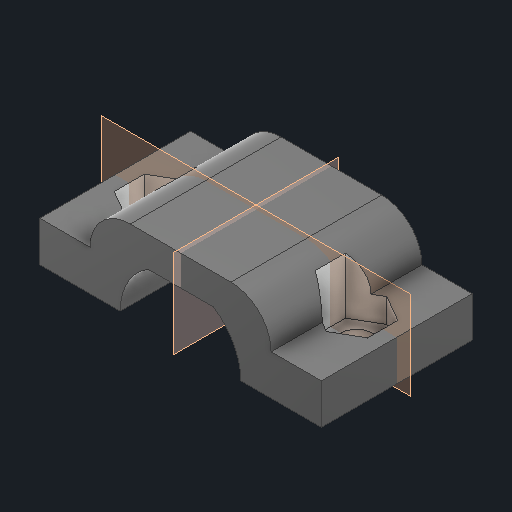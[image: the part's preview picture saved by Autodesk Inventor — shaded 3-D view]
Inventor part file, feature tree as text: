
AUTODESK INVENTOR PART (.ipt)
format: ipt  version: 2024 (Build 280153000, 153)  size: 161,792 bytes
history: native  units: in
note: dims shown in document units (in); Inventor stores cm internally (conversion verified against a paired STEP export)
features: other x3, plane x2, sketch x1
ambient origin geometry x8: Origin, YZ Plane, XZ Plane, XY Plane, X Axis, Y Axis, Z Axis, Center Point
bodies: Solid1 (feature_tree)
feature tree (6):
  other  "mocowanie_silnika.ipt"
  other  "Solid1::mocowanie_silnika.ipt"
  other  "TaggingFeature1"
  sketch  "Sketch5"  dims[d0=0.3937in]
  plane  "Work Plane1"
  plane  "Work Plane2"
